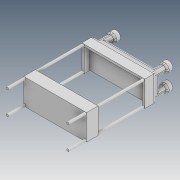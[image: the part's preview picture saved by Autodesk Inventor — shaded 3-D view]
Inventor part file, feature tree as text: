
AUTODESK INVENTOR PART (.ipt)
format: ipt  version: 2021 (Build 250183000, 183)  size: 530,944 bytes
history: native  units: in
note: dims shown in document units (in); Inventor stores cm internally (conversion verified against a paired STEP export)
features: extrude x7, sketch x7, fillet x3, other x1
ambient origin geometry x8: Origin, YZ Plane, XZ Plane, XY Plane, X Axis, Y Axis, Z Axis, Center Point
bodies: Body1 (feature_tree), Body2 (feature_tree)
feature tree (18):
  other  "Sólido1"
  extrude  "Extrusão1"  Depth=0.7874in
  extrude  "Extrusão2"  Depth=0.1969in
  extrude  "Extrusão3"  Depth=0.3937in TaperAngle=0.0deg
  extrude  "Extrusão4"  Depth=0.8661in
  extrude  "Extrusão5"  Depth=0.3937in TaperAngle=0.0deg
  extrude  "Extrusão6"  Depth=0.0787in
  fillet  "Arredondamento1"  Radius=0.0787in
  fillet  "Arredondamento2"  Radius=0.0787in
  extrude  "Extrusão7"  Depth=1.5748in TaperAngle=0.0deg
  fillet  "Arredondamento3"  Radius=0.3937in
  sketch  "Esboço1"  dims[d0=1.9685in d1=0.7874in]
  sketch  "Esboço2"  dims[d2=0.3937in d3=0.0in d4=0.1969in]
  sketch  "Esboço3"  dims[d5=0.1969in d6=0.3937in d7=0.0in]
  sketch  "Esboço5"  dims[d8=0.0787in d9=0.8661in]
  sketch  "Esboço9"  dims[d10=2.126in d11=0.3937in d12=0.0in]
  sketch  "Esboço10"  dims[d13=0.0787in d14=0.0787in d15=0.0787in d16=0.0787in]
  sketch  "Esboço11"  dims[d17=0.0787in d18=1.5748in d19=0.0in d29=0.3937in d30=0.8661in d31=0.0in d32=0.0787in d33=0.5906in d34=0.0in d35=0.0787in d36=0.0787in d37=0.2953in d38=0.2953in d39=1.063in d40=0.1969in d41=0.0in d42=0.0787in d43=0.0344in]
